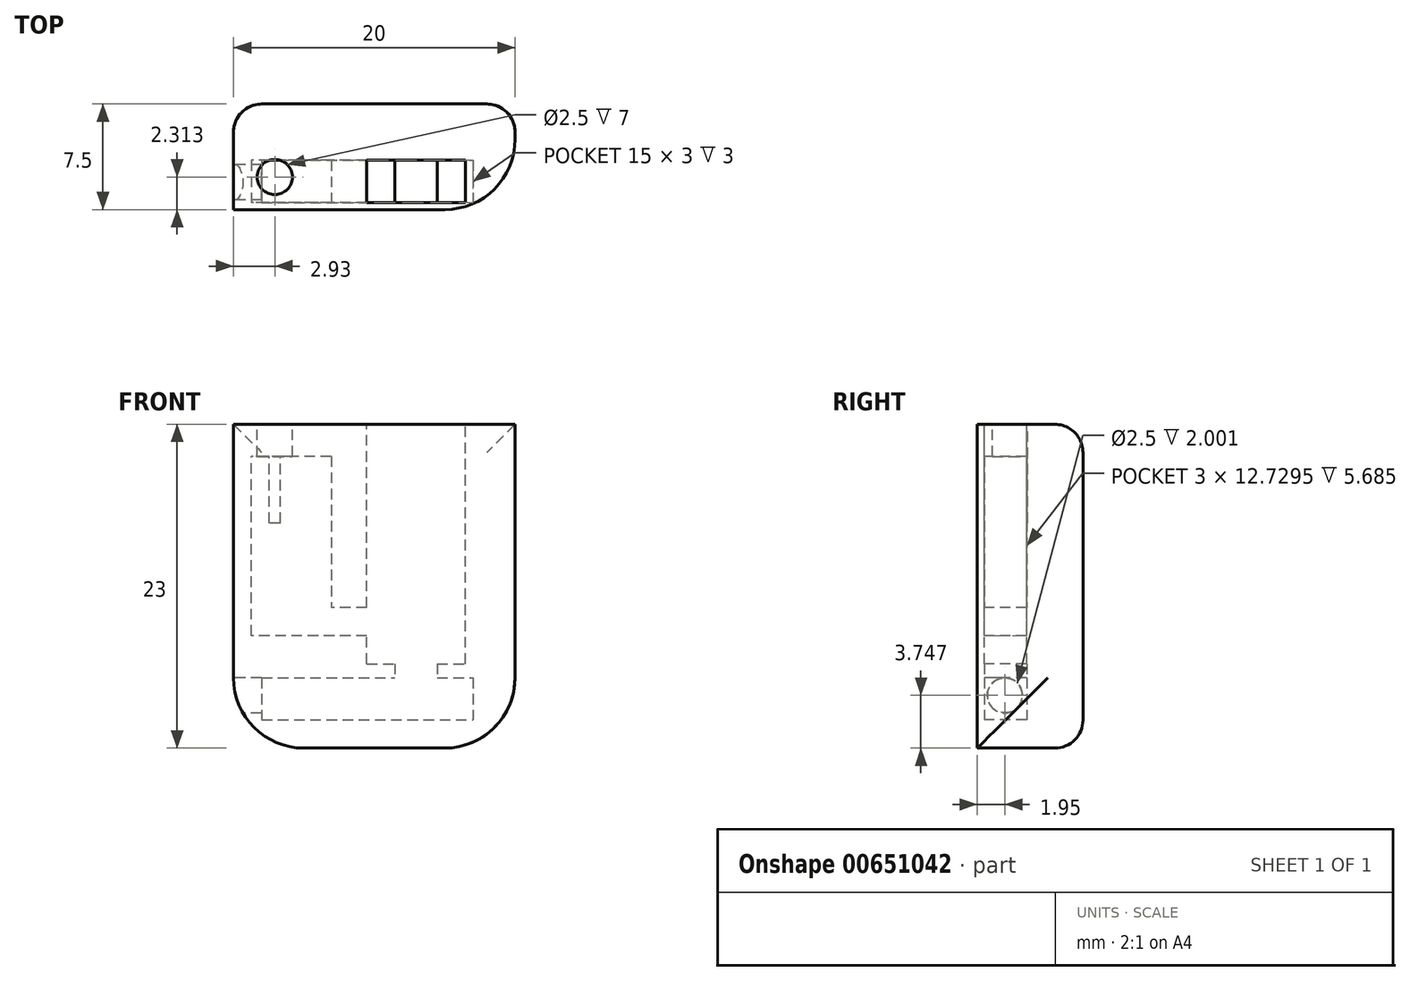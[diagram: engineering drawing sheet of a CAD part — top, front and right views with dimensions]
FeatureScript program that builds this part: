
annotation { "Feature Type Name" : "Feature", "Feature Type Description" : "" }
export const myFeature = defineFeature(function(context is Context, id is Id, definition is map)
    precondition{}
    {
        {
            var Q0;
            Q0=qCreatedBy(makeId("Front.planeOp"),FACE);
            var sketch = newSketch(context, id + "F0", { "sketchPlane" : qUnion([Q0])});
            skLineSegment(sketch, "E0.bottom", {"start": v(-19.51, 27.82) * mm, "end": v(0.49, 27.82) * mm});
            skLineSegment(sketch, "E0.top", {"start": v(-19.51, 4.82) * mm, "end": v(0.49, 4.82) * mm});
            skLineSegment(sketch, "E0.left", {"start": v(-19.51, 27.82) * mm, "end": v(-19.51, 4.82) * mm});
            skLineSegment(sketch, "E0.right", {"start": v(0.49, 27.82) * mm, "end": v(0.49, 4.82) * mm});
            skSolve(sketch);
        }
        {
            var Q0;
            Q0 = qSketchRegion(id + "F0", true);
            extrude(context, id + "F1", {"entities" : qUnion([Q0]), "depth" : 7 * mm, "offsetDistance" : 25 * mm});
        }
        {
            var Q0;
            Q0=makeQuery(id+"F1.opExtrude","CAP_FACE",FACE,{"disambiguationData":[OSD([sQuery(id+"F0.wireOp",EDGE,"E0.bottom"),sQuery(id+"F0.wireOp",EDGE,"E0.top"),sQuery(id+"F0.wireOp",EDGE,"E0.left"),sQuery(id+"F0.wireOp",EDGE,"E0.right")])],"isStart":false});
            var sketch = newSketch(context, id + "F2", { "sketchPlane" : qUnion([Q0])});
            skLineSegment(sketch, "E1.bottom", {"start": v(-17.51, 9.82) * mm, "end": v(-2.51, 9.82) * mm});
            skLineSegment(sketch, "E1.top", {"start": v(-17.51, 6.82) * mm, "end": v(-2.51, 6.82) * mm});
            skLineSegment(sketch, "E1.left", {"start": v(-17.51, 9.82) * mm, "end": v(-17.51, 6.82) * mm});
            skLineSegment(sketch, "E1.right", {"start": v(-2.51, 9.82) * mm, "end": v(-2.51, 6.82) * mm});
            skSolve(sketch);
        }
        {
            var Q0;
            Q0 = qSketchRegion(id + "F2", true);
            extrude(context, id + "F3", {"entities" : qUnion([Q0]), "operationType" : NewBodyOperationType.REMOVE, "oppositeDirection" : true, "depth" : 3 * mm, "offsetDistance" : 25 * mm});
        }
        {
            var Q0;
            Q0=makeQuery(id+"F1.opExtrude","CAP_FACE",FACE,{"disambiguationData":[OSD([sQuery(id+"F0.wireOp",EDGE,"E0.bottom"),sQuery(id+"F0.wireOp",EDGE,"E0.top"),sQuery(id+"F0.wireOp",EDGE,"E0.left"),sQuery(id+"F0.wireOp",EDGE,"E0.right")])],"isStart":false});
            var sketch = newSketch(context, id + "F4", { "sketchPlane" : qUnion([Q0])});
            skLineSegment(sketch, "E2.bottom", {"start": v(-10.05, 10.82) * mm, "end": v(-3.05, 10.82) * mm});
            skLineSegment(sketch, "E2.top", {"start": v(-10.05, 27.82) * mm, "end": v(-3.05, 27.82) * mm});
            skLineSegment(sketch, "E2.left", {"start": v(-10.05, 10.82) * mm, "end": v(-10.05, 27.82) * mm});
            skLineSegment(sketch, "E2.right", {"start": v(-3.05, 10.82) * mm, "end": v(-3.05, 27.82) * mm});
            skSolve(sketch);
        }
        {
            var Q0;
            Q0 = qSketchRegion(id + "F4", true);
            extrude(context, id + "F5", {"entities" : qUnion([Q0]), "operationType" : NewBodyOperationType.REMOVE, "oppositeDirection" : true, "depth" : 3 * mm, "offsetDistance" : 25 * mm});
        }
        {
            var Q0;
            Q0=makeQuery(id+"F1.opExtrude","CAP_FACE",FACE,{"disambiguationData":[OSD([sQuery(id+"F0.wireOp",EDGE,"E0.bottom"),sQuery(id+"F0.wireOp",EDGE,"E0.top"),sQuery(id+"F0.wireOp",EDGE,"E0.left"),sQuery(id+"F0.wireOp",EDGE,"E0.right")])],"isStart":false});
            var sketch = newSketch(context, id + "F6", { "sketchPlane" : qUnion([Q0])});
            skLineSegment(sketch, "E3.bottom", {"start": v(-8.05, 10.82) * mm, "end": v(-5.05, 10.82) * mm});
            skLineSegment(sketch, "E3.top", {"start": v(-8.05, 9.82) * mm, "end": v(-5.05, 9.82) * mm});
            skLineSegment(sketch, "E3.left", {"start": v(-8.05, 10.82) * mm, "end": v(-8.05, 9.82) * mm});
            skLineSegment(sketch, "E3.right", {"start": v(-5.05, 10.82) * mm, "end": v(-5.05, 9.82) * mm});
            skSolve(sketch);
        }
        {
            var Q0;
            Q0 = qSketchRegion(id + "F6", true);
            extrude(context, id + "F7", {"entities" : qUnion([Q0]), "operationType" : NewBodyOperationType.REMOVE, "oppositeDirection" : true, "depth" : 3 * mm, "offsetDistance" : 25 * mm});
        }
        {
            var Q0;
            Q0=makeQuery(id+"F1.opExtrude","CAP_FACE",FACE,{"disambiguationData":[OSD([sQuery(id+"F0.wireOp",EDGE,"E0.bottom"),sQuery(id+"F0.wireOp",EDGE,"E0.top"),sQuery(id+"F0.wireOp",EDGE,"E0.left"),sQuery(id+"F0.wireOp",EDGE,"E0.right")])],"isStart":false});
            var sketch = newSketch(context, id + "F8", { "sketchPlane" : qUnion([Q0])});
            skLineSegment(sketch, "E4.bottom", {"start": v(-10.05, 14.82) * mm, "end": v(-12.57, 14.82) * mm});
            skLineSegment(sketch, "E4.top", {"start": v(-10.05, 12.82) * mm, "end": v(-12.57, 12.82) * mm});
            skLineSegment(sketch, "E4.left", {"start": v(-10.05, 14.82) * mm, "end": v(-10.05, 12.82) * mm});
            skLineSegment(sketch, "E4.right", {"start": v(-12.57, 14.82) * mm, "end": v(-12.57, 12.82) * mm});
            skSolve(sketch);
        }
        {
            var Q0;
            Q0 = qSketchRegion(id + "F8", true);
            extrude(context, id + "F9", {"entities" : qUnion([Q0]), "operationType" : NewBodyOperationType.REMOVE, "oppositeDirection" : true, "depth" : 3 * mm, "offsetDistance" : 25 * mm});
        }
        {
            var Q0;
            Q0=makeQuery(id+"F1.opExtrude","SWEPT_FACE",FACE,{"disambiguationData":[OSD([sQuery(id+"F0.wireOp",EDGE,"E0.left")])]});
            var sketch = newSketch(context, id + "F10", { "sketchPlane" : qUnion([Q0])});
            skCircle(sketch, "E5", {"center": v(5.55, 8.57) * mm, "radius": 1.25 * mm});
            skSolve(sketch);
        }
        {
            var Q0;
            Q0 = qSketchRegion(id + "F10", true);
            extrude(context, id + "F11", {"entities" : qUnion([Q0]), "operationType" : NewBodyOperationType.REMOVE, "oppositeDirection" : true, "depth" : 5 * mm, "offsetDistance" : 25 * mm});
        }
        {
            var Q0;
            Q0=makeQuery(id+"F1.opExtrude","CAP_EDGE",EDGE,{"disambiguationData":[OSD([sQuery(id+"F0.wireOp",EDGE,"E0.right")])],"isStart":true});
            var Q1;
            Q1=makeQuery(id+"F1.opExtrude","CAP_EDGE",EDGE,{"disambiguationData":[OSD([sQuery(id+"F0.wireOp",EDGE,"E0.left")])],"isStart":true});
            var Q2;
            Q2=makeQuery(id+"F1.opExtrude","CAP_EDGE",EDGE,{"disambiguationData":[OSD([sQuery(id+"F0.wireOp",EDGE,"E0.bottom")])],"isStart":true});
            var Q3;
            Q3=makeQuery(id+"F1.opExtrude","CAP_EDGE",EDGE,{"disambiguationData":[OSD([sQuery(id+"F0.wireOp",EDGE,"E0.top")])],"isStart":true});
            fillet(context, id + "F12", {"entities" : qUnion([Q0, Q1, Q2, Q3]), "radius" : 2 * mm, "tangentPropagation" : true, "allowEdgeOverflow" : false});
        }
        {
            var Q0;
            Q0=makeQuery(id+"F1.opExtrude","CAP_FACE",FACE,{"disambiguationData":[OSD([sQuery(id+"F0.wireOp",EDGE,"E0.bottom"),sQuery(id+"F0.wireOp",EDGE,"E0.top"),sQuery(id+"F0.wireOp",EDGE,"E0.left"),sQuery(id+"F0.wireOp",EDGE,"E0.right")])],"isStart":false});
            var sketch = newSketch(context, id + "F13", { "sketchPlane" : qUnion([Q0])});
            skLineSegment(sketch, "E6.bottom", {"start": v(-12.57, 12.82) * mm, "end": v(-18.26, 12.82) * mm});
            skLineSegment(sketch, "E6.top", {"start": v(-12.57, 25.55) * mm, "end": v(-18.26, 25.55) * mm});
            skLineSegment(sketch, "E6.left", {"start": v(-12.57, 12.82) * mm, "end": v(-12.57, 25.55) * mm});
            skLineSegment(sketch, "E6.right", {"start": v(-18.26, 12.82) * mm, "end": v(-18.26, 25.55) * mm});
            skSolve(sketch);
        }
        {
            var Q0;
            Q0 = qSketchRegion(id + "F13", true);
            extrude(context, id + "F14", {"entities" : qUnion([Q0]), "operationType" : NewBodyOperationType.REMOVE, "oppositeDirection" : true, "depth" : 3 * mm, "offsetDistance" : 25 * mm});
        }
        {
            var Q0;
            Q0=makeQuery(id+"F1.opExtrude","CAP_FACE",FACE,{"disambiguationData":[OSD([sQuery(id+"F0.wireOp",EDGE,"E0.bottom"),sQuery(id+"F0.wireOp",EDGE,"E0.top"),sQuery(id+"F0.wireOp",EDGE,"E0.left"),sQuery(id+"F0.wireOp",EDGE,"E0.right")])],"isStart":false});
            var sketch = newSketch(context, id + "F15", { "sketchPlane" : qUnion([Q0])});
            skLineSegment(sketch, "E7.bottom", {"start": v(-19.51, 27.82) * mm, "end": v(0.49, 27.82) * mm});
            skLineSegment(sketch, "E7.top", {"start": v(-19.51, 4.82) * mm, "end": v(0.49, 4.82) * mm});
            skLineSegment(sketch, "E7.left", {"start": v(-19.51, 27.82) * mm, "end": v(-19.51, 4.82) * mm});
            skLineSegment(sketch, "E7.right", {"start": v(0.49, 27.82) * mm, "end": v(0.49, 4.82) * mm});
            skSolve(sketch);
        }
        {
            var Q0;
            Q0 = qSketchRegion(id + "F15", true);
            extrude(context, id + "F16", {"entities" : qUnion([Q0]), "operationType" : NewBodyOperationType.ADD, "depth" : 0.5 * mm, "offsetDistance" : 25 * mm});
        }
        {
            var Q0;
            Q0=makeQuery(id+"F16.boolean.opBoolean","MERGE",EDGE,{"derivedFrom":[makeQuery(id+"F1.opExtrude","SWEPT_EDGE",EDGE,{"disambiguationData":[OSD([sQuery(id+"F0.wireOp",EDGE,"E0.top"),sQuery(id+"F0.wireOp",EDGE,"E0.left")])]}),makeQuery(id+"F16.opExtrude","SWEPT_EDGE",EDGE,{"disambiguationData":[OSD([sQuery(id+"F15.wireOp",EDGE,"E7.top"),sQuery(id+"F15.wireOp",EDGE,"E7.left")])]})]});
            var Q1;
            Q1=makeQuery(id+"F16.boolean.opBoolean","MERGE",EDGE,{"derivedFrom":[makeQuery(id+"F1.opExtrude","SWEPT_EDGE",EDGE,{"disambiguationData":[OSD([sQuery(id+"F0.wireOp",EDGE,"E0.top"),sQuery(id+"F0.wireOp",EDGE,"E0.right")])]}),makeQuery(id+"F16.opExtrude","SWEPT_EDGE",EDGE,{"disambiguationData":[OSD([sQuery(id+"F15.wireOp",EDGE,"E7.top"),sQuery(id+"F15.wireOp",EDGE,"E7.right")])]})]});
            var Q2;
            Q2=makeQuery(id+"F16.opExtrude","CAP_EDGE",EDGE,{"disambiguationData":[OSD([sQuery(id+"F15.wireOp",EDGE,"E7.right")])],"isStart":false});
            fillet(context, id + "F17", {"entities" : qUnion([Q0, Q1, Q2]), "radius" : 5 * mm, "tangentPropagation" : true, "allowEdgeOverflow" : false});
        }
        {
            var Q0;
            Q0=makeQuery(id+"F16.boolean.opBoolean","MERGE",FACE,{"derivedFrom":[makeQuery(id+"F1.opExtrude","SWEPT_FACE",FACE,{"disambiguationData":[OSD([sQuery(id+"F0.wireOp",EDGE,"E0.bottom")])]}),makeQuery(id+"F16.opExtrude","SWEPT_FACE",FACE,{"disambiguationData":[OSD([sQuery(id+"F15.wireOp",EDGE,"E7.bottom")])]})]});
            var sketch = newSketch(context, id + "F18", { "sketchPlane" : qUnion([Q0])});
            skCircle(sketch, "E8", {"center": v(-16.58, -5.19) * mm, "radius": 1.25 * mm});
            skSolve(sketch);
        }
        {
            var Q0;
            Q0 = qSketchRegion(id + "F18", true);
            extrude(context, id + "F19", {"entities" : qUnion([Q0]), "operationType" : NewBodyOperationType.REMOVE, "oppositeDirection" : true, "depth" : 7 * mm, "offsetDistance" : 25 * mm});
        }
    });
